FCSTD DOCUMENT  (FreeCAD 0.21R33675 (Git))
Label: reed_slip_calculator
License: Creative Commons Attribution-NoDerivatives 3.0
objects: Sketcher::SketchObject×6, App::DocumentObjectGroup×1
note: 6 computed .brp shape members not serialized (recipe doc carries the construction recipe); baked Part::Feature solids carry a one-line shape summary decoded from their .brp

FEATURE [Sketcher::SketchObject] Sketch  label="calculate_cylinderOD_caneOD_from_dip_centerline_width"
  FullyConstrained = true
  Placement = pos=(0,0,0) rot=(1,0,0;1.5708rad)
  sketch-geometry (7):
    g0: LineSegment StartX=-5 StartY=0 StartZ=0 EndX=5 EndY=0 EndZ=0
    g1: ArcOfCircle CenterX=-3e-16 CenterY=-5.97227 CenterZ=0 NormalX=0 NormalY=0 NormalZ=1 AngleXU=0 Radius=7.98227 StartAngle=0.893885 EndAngle=2.24771
    g2: ArcOfCircle CenterX=1.8e-15 CenterY=-17.5071 CenterZ=0 NormalX=0 NormalY=0 NormalZ=1 AngleXU=0 Radius=18.2071 StartAngle=1.2926 EndAngle=1.84899
    g3: GeomPoint X=0 Y=0.7 Z=0
    g4: GeomPoint X=0 Y=2.01 Z=0
    g5: LineSegment StartX=-5 StartY=0.25 StartZ=0 EndX=-5 EndY=0 EndZ=0
    g6: LineSegment StartX=5 StartY=0.25 StartZ=0 EndX=5 EndY=0 EndZ=0
  constraints (22):
    c: DistanceX(g0,g0) = 10  'width'
    c: PointOnObject(g3,g-2)
    c: PointOnObject(g4,g-2)
    c: PointOnObject(g3,g2)
    c: PointOnObject(g4,g1)
    c: Diameter(g1) = 15.9645  'cane_OD'
    c: Diameter(g2) = 36.4143  'cylinder_OD'
    c: Coincident(g5,g1)
    c: Coincident(g5,g2)
    c: Vertical(g5)
    c: Coincident(g6,g1)
    c: Coincident(g6,g2)
    c: Vertical(g6)
    c: Coincident(g0,g2)
    c: PointOnObject(g2,g-1)
    c: Coincident(g2,g0)
    c: Equal(g6,g5)
    c: Symmetric(g2,g2,g-1)
    c: DistanceY(g6,g6) = 0.25  'edge_thickness'
    c: DistanceY(g-1,g3) = 0.7  'dip'
    c: DistanceY(g3,g4) = 1.31  'centerline'
    c: DistanceY(g-1,g4) = 2.01  'stature'
FEATURE [Sketcher::SketchObject] Sketch001  label="calculate_dip_centerline_from_caneOD_cylinderOD_width"
  FullyConstrained = true
  Placement = pos=(0,0,0) rot=(1,0,0;1.5708rad)
  sketch-geometry (7):
    g0: LineSegment StartX=-6.25 StartY=7.1e-15 StartZ=0 EndX=6.25 EndY=7.1e-15 EndZ=0
    g1: ArcOfCircle CenterX=-8e-16 CenterY=-10.5753 CenterZ=0 NormalX=0 NormalY=0 NormalZ=1 AngleXU=0 Radius=12.5 StartAngle=1.0472 EndAngle=2.0944
    g2: ArcOfCircle CenterX=5.9e-15 CenterY=-34.4374 CenterZ=0 NormalX=0 NormalY=0 NormalZ=1 AngleXU=0 Radius=35 StartAngle=1.39126 EndAngle=1.75033
    g3: GeomPoint X=0 Y=0.562557 Z=0
    g4: GeomPoint X=0 Y=1.92468 Z=0
    g5: LineSegment StartX=-6.25 StartY=0.25 StartZ=0 EndX=-6.25 EndY=7.1e-15 EndZ=0
    g6: LineSegment StartX=6.25 StartY=0.25 StartZ=0 EndX=6.25 EndY=7.1e-15 EndZ=0
  constraints (22):
    c: DistanceX(g0,g0) = 12.5  'width'
    c: PointOnObject(g3,g-2)
    c: PointOnObject(g4,g-2)
    c: PointOnObject(g3,g2)
    c: PointOnObject(g4,g1)
    c: Diameter(g1) = 25  'cane_OD'
    c: Diameter(g2) = 70  'cylinder_OD'
    c: Coincident(g5,g1)
    c: Coincident(g5,g2)
    c: Vertical(g5)
    c: Coincident(g6,g1)
    c: Coincident(g6,g2)
    c: Vertical(g6)
    c: Coincident(g0,g2)
    c: PointOnObject(g2,g-1)
    c: Coincident(g2,g0)
    c: Equal(g6,g5)
    c: Symmetric(g2,g2,g-1)
    c: DistanceY(g6,g6) = 0.25  'edge_thickness'
    c: DistanceY(g-1,g3) = 0.562557  'dip'
    c: DistanceY(g3,g4) = 1.36213  'centerline'
    c: DistanceY(g-1,g4) = 1.92468  'stature'
FEATURE [Sketcher::SketchObject] Sketch002  label="calc_caneOD_dip_centerline_from_width_cylinderOD_FromentRuleOfThirds"
  FullyConstrained = true
  Placement = pos=(0,0,0) rot=(1,0,0;1.5708rad)
  expr: .Constraints.centerline = 2 * .Constraints.dip
  sketch-geometry (7):
    g0: LineSegment StartX=-6.25 StartY=0 StartZ=0 EndX=6.25 EndY=3.6e-15 EndZ=0
    g1: ArcOfCircle CenterX=-2e-16 CenterY=-10.2114 CenterZ=0 NormalX=0 NormalY=0 NormalZ=1 AngleXU=0 Radius=12.1862 StartAngle=1.03227 EndAngle=2.10933
    g2: ArcOfCircle CenterX=3.3e-15 CenterY=-29.3417 CenterZ=0 NormalX=0 NormalY=0 NormalZ=1 AngleXU=0 Radius=30 StartAngle=1.36093 EndAngle=1.78067
    g3: GeomPoint X=0 Y=0.658264 Z=0
    g4: GeomPoint X=0 Y=1.97479 Z=0
    g5: LineSegment StartX=-6.25 StartY=0.25 StartZ=0 EndX=-6.25 EndY=0 EndZ=0
    g6: LineSegment StartX=6.25 StartY=0.25 StartZ=0 EndX=6.25 EndY=3.6e-15 EndZ=0
  constraints (22):
    c: DistanceX(g0,g0) = 12.5  'width'
    c: PointOnObject(g3,g-2)
    c: PointOnObject(g4,g-2)
    c: PointOnObject(g3,g2)
    c: PointOnObject(g4,g1)
    c: Diameter(g1) = 24.3725  'cane_OD'
    c: Diameter(g2) = 60  'cylinder_OD'
    c: Coincident(g5,g1)
    c: Coincident(g5,g2)
    c: Vertical(g5)
    c: Coincident(g6,g1)
    c: Coincident(g6,g2)
    c: Vertical(g6)
    c: Coincident(g0,g2)
    c: PointOnObject(g2,g-1)
    c: Coincident(g2,g0)
    c: Equal(g6,g5)
    c: Symmetric(g2,g2,g-1)
    c: DistanceY(g6,g6) = 0.25  'edge_thickness'
    c: DistanceY(g-1,g3) = 0.658264  'dip'
    c: DistanceY(g3,g4) = 1.31653  'centerline'
    c: DistanceY(g-1,g4) = 1.97479  'stature'
FEATURE [Sketcher::SketchObject] Sketch003  label="calc_cylinderOD_dip_centerline_from_width_caneOD_FromentRuleOfThirds"
  FullyConstrained = true
  Placement = pos=(0,0,0) rot=(1,0,0;1.5708rad)
  expr: .Constraints.dip = .Constraints.centerline / 2
  sketch-geometry (7):
    g0: LineSegment StartX=-6.5 StartY=0 StartZ=0 EndX=6.5 EndY=0 EndZ=0
    g1: ArcOfCircle CenterX=-3e-16 CenterY=-11.0083 CenterZ=0 NormalX=0 NormalY=0 NormalZ=1 AngleXU=0 Radius=13 StartAngle=1.0472 EndAngle=2.0944
    g2: ArcOfCircle CenterX=1.62e-14 CenterY=-34.0185 CenterZ=0 NormalX=0 NormalY=0 NormalZ=1 AngleXU=0 Radius=34.634 StartAngle=1.382 EndAngle=1.75959
    g3: GeomPoint X=0 Y=0.615418 Z=0
    g4: GeomPoint X=0 Y=1.99167 Z=0
    g5: LineSegment StartX=-6.5 StartY=0.25 StartZ=0 EndX=-6.5 EndY=0 EndZ=0
    g6: LineSegment StartX=6.5 StartY=0.25 StartZ=0 EndX=6.5 EndY=0 EndZ=0
  constraints (22):
    c: DistanceX(g0,g0) = 13  'width'
    c: PointOnObject(g3,g-2)
    c: PointOnObject(g4,g-2)
    c: PointOnObject(g3,g2)
    c: PointOnObject(g4,g1)
    c: Diameter(g1) = 26  'cane_OD'
    c: Diameter(g2) = 69.2679  'cylinder_OD'
    c: Coincident(g5,g1)
    c: Coincident(g5,g2)
    c: Vertical(g5)
    c: Coincident(g6,g1)
    c: Coincident(g6,g2)
    c: Vertical(g6)
    c: Coincident(g0,g2)
    c: PointOnObject(g2,g-1)
    c: Coincident(g2,g0)
    c: Equal(g6,g5)
    c: Symmetric(g2,g2,g-1)
    c: DistanceY(g6,g6) = 0.25  'edge_thickness'
    c: DistanceY(g-1,g3) = 0.615418  'dip'
    c: DistanceY(g3,g4) = 1.37625  'centerline'
    c: DistanceY(g-1,g4) = 1.99167  'stature'
FEATURE [Sketcher::SketchObject] Sketch004  label="calc_width_centerline_from_cylinderOD_dip_caneOD"
  FullyConstrained = true
  Placement = pos=(0,0,0) rot=(1,0,0;1.5708rad)
  sketch-geometry (7):
    g0: LineSegment StartX=-6.18041 StartY=0 StartZ=0 EndX=6.18041 EndY=0 EndZ=0
    g1: ArcOfCircle CenterX=2e-16 CenterY=-10.6152 CenterZ=0 NormalX=0 NormalY=0 NormalZ=1 AngleXU=0 Radius=12.5 StartAngle=1.05361 EndAngle=2.08798
    g2: ArcOfCircle CenterX=-1.42e-14 CenterY=-34.45 CenterZ=0 NormalX=0 NormalY=0 NormalZ=1 AngleXU=0 Radius=35 StartAngle=1.39328 EndAngle=1.74831
    g3: GeomPoint X=0 Y=0.55 Z=0
    g4: GeomPoint X=0 Y=1.8848 Z=0
    g5: LineSegment StartX=-6.18041 StartY=0.25 StartZ=0 EndX=-6.18041 EndY=0 EndZ=0
    g6: LineSegment StartX=6.18041 StartY=0.25 StartZ=0 EndX=6.18041 EndY=0 EndZ=0
  constraints (22):
    c: DistanceX(g0,g0) = 12.3608  'width'
    c: PointOnObject(g3,g-2)
    c: PointOnObject(g4,g-2)
    c: PointOnObject(g3,g2)
    c: PointOnObject(g4,g1)
    c: Diameter(g1) = 25  'cane_OD'
    c: Diameter(g2) = 70  'cylinder_OD'
    c: Coincident(g5,g1)
    c: Coincident(g5,g2)
    c: Vertical(g5)
    c: Coincident(g6,g1)
    c: Coincident(g6,g2)
    c: Vertical(g6)
    c: Coincident(g0,g2)
    c: PointOnObject(g2,g-1)
    c: Coincident(g2,g0)
    c: Equal(g6,g5)
    c: Symmetric(g2,g2,g-1)
    c: DistanceY(g6,g6) = 0.25  'edge_thickness'
    c: DistanceY(g-1,g3) = 0.55  'dip'
    c: DistanceY(g3,g4) = 1.3348  'centerline'
    c: DistanceY(g-1,g4) = 1.8848  'stature'
FEATURE [App::DocumentObjectGroup] Group  label="slip_calculations"
  Group = -> [Sketch001,Sketch,Sketch002,Sketch003,Sketch004]
FEATURE [Sketcher::SketchObject] Sketch005  label="Froment_Rule_of_Thirds"
  FullyConstrained = false
  Placement = pos=(0,0,0) rot=(1,0,0;1.5708rad)
  expr: .Constraints.aperture = .Constraints.total_depth / 3
  sketch-geometry (13):
    g0: LineSegment StartX=-5 StartY=0 StartZ=0 EndX=5 EndY=0 EndZ=0
    g1: ArcOfCircle CenterX=8e-16 CenterY=-8.84076 CenterZ=0 NormalX=0 NormalY=0 NormalZ=1 AngleXU=0 Radius=10.3751 StartAngle=1.06795 EndAngle=2.07365
    g2: ArcOfCircle CenterX=1.1e-15 CenterY=-24.1854 CenterZ=0 NormalX=0 NormalY=0 NormalZ=1 AngleXU=0 Radius=24.6968 StartAngle=1.36693 EndAngle=1.77466
    g3: GeomPoint X=0 Y=0.511434 Z=0
    g4: GeomPoint X=0 Y=1.5343 Z=0
    g5: LineSegment StartX=-5 StartY=0.25 StartZ=0 EndX=-5 EndY=0 EndZ=0
    g6: LineSegment StartX=5 StartY=0.25 StartZ=0 EndX=5 EndY=0 EndZ=0
    g7: ArcOfCircle CenterX=2.6e-15 CenterY=24.1854 CenterZ=0 NormalX=0 NormalY=0 NormalZ=1 AngleXU=0 Radius=24.6968 StartAngle=4.50852 EndAngle=4.91625
    g8: GeomPoint X=0 Y=-0.511434 Z=0
    g9: LineSegment StartX=5 StartY=0 StartZ=0 EndX=5 EndY=-0.25 EndZ=0
    g10: LineSegment StartX=-5 StartY=0 StartZ=0 EndX=-5 EndY=-0.25 EndZ=0
    g11: ArcOfCircle CenterX=-1.6e-15 CenterY=8.84076 CenterZ=0 NormalX=0 NormalY=0 NormalZ=1 AngleXU=0 Radius=10.3751 StartAngle=4.20954 EndAngle=5.21524
    g12: GeomPoint X=0 Y=-1.5343 Z=0
  constraints (33):
    c: PointOnObject(g3,g-2)
    c: PointOnObject(g4,g-2)
    c: PointOnObject(g3,g2)
    c: PointOnObject(g4,g1)
    c: Coincident(g5,g1)
    c: Coincident(g5,g2)
    c: Vertical(g5)
    c: Coincident(g6,g1)
    c: Coincident(g6,g2)
    c: Vertical(g6)
    c: Coincident(g0,g2)
    c: PointOnObject(g2,g-1)
    c: Coincident(g2,g0)
    c: Equal(g6,g5)
    c: Symmetric(g2,g2,g-1)
    c: Coincident(g7,g2)
    c: Coincident(g7,g2)
    c: PointOnObject(g8,g7)
    c: DistanceX(g0,g0) = 10  'width'
    c: Symmetric(g3,g8,g-1)
    c: Coincident(g9,g2)
    c: Vertical(g9)
    c: Coincident(g10,g2)
    c: Vertical(g10)
    c: Equal(g5,g10)
    c: Equal(g9,g10)
    c: Coincident(g11,g10)
    c: Coincident(g11,g9)
    c: PointOnObject(g12,g11)
    c: Symmetric(g4,g12,g-1)
    c: DistanceY(g6,g6) = 0.25  'edge_thickness'
    c: DistanceY(g8,g3) = 1.02287  'aperture'
    c: DistanceY(g12,g4) = 3.06861  'total_depth'
